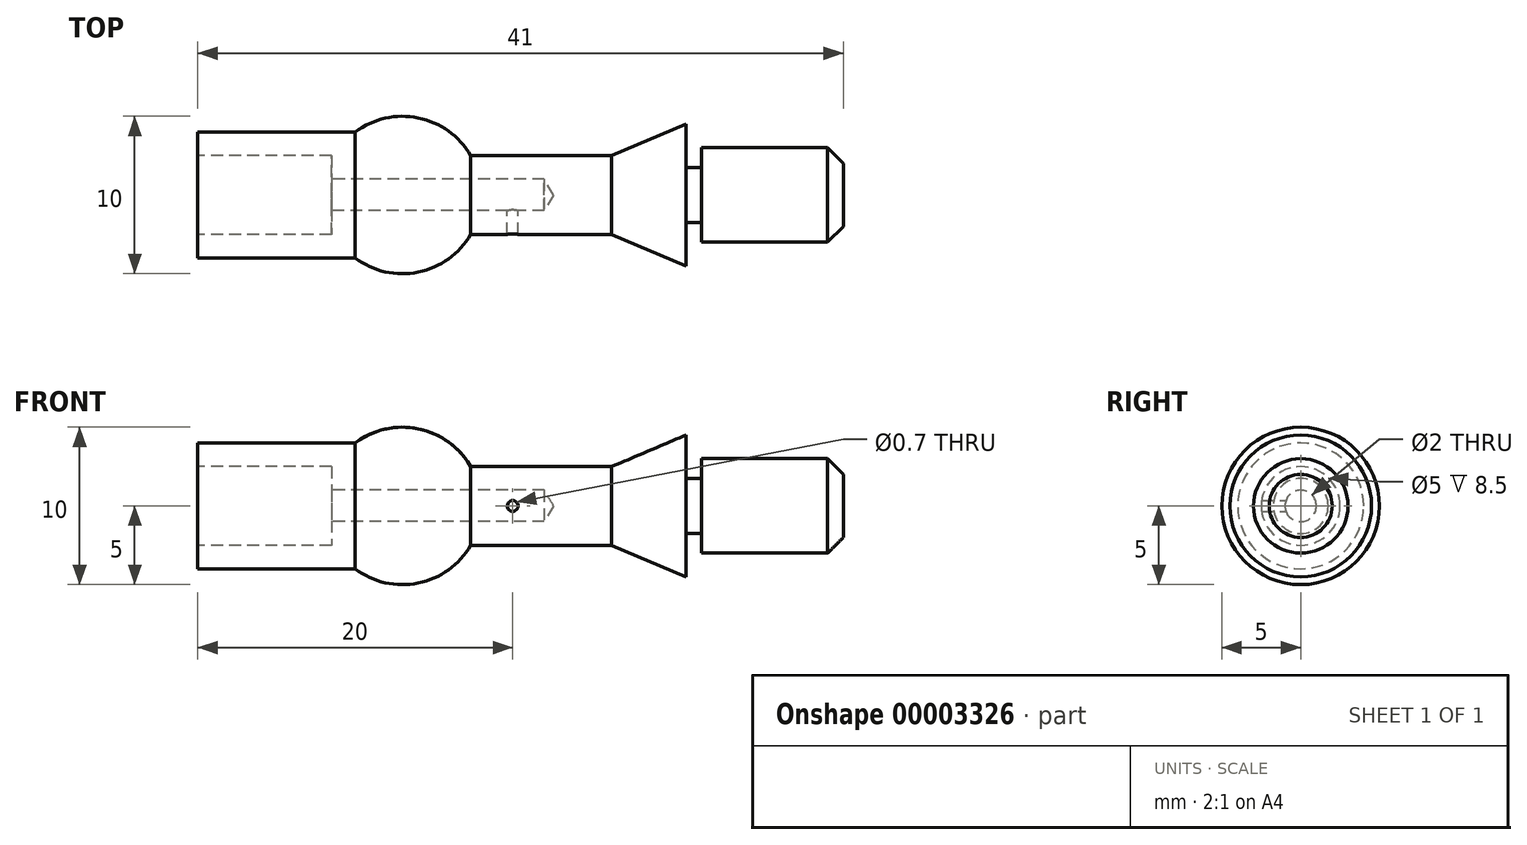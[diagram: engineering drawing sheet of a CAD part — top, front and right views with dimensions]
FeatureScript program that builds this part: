
annotation { "Feature Type Name" : "Feature", "Feature Type Description" : "" }
export const myFeature = defineFeature(function(context is Context, id is Id, definition is map)
    precondition{}
    {
        {
            var Q0;
            Q0=qCreatedBy(makeId("Front.planeOp"),FACE);
            var sketch = newSketch(context, id + "F0", { "sketchPlane" : qUnion([Q0])});
            skLineSegment(sketch, "E0", {"start": v(0, 0) * mm, "end": v(41, 0) * mm, "construction": true});
            skLineSegment(sketch, "E1", {"start": v(0, 2.5) * mm, "end": v(0, 4) * mm});
            skLineSegment(sketch, "E2", {"start": v(0, 4) * mm, "end": v(10, 4) * mm});
            skLineSegment(sketch, "E3", {"start": v(0, 2.5) * mm, "end": v(8.5, 2.5) * mm});
            skLineSegment(sketch, "E4", {"start": v(8.5, 2.5) * mm, "end": v(8.5, 1) * mm});
            skLineSegment(sketch, "E5", {"start": v(8.5, 1) * mm, "end": v(22, 1) * mm});
            skArc(sketch, "E6", {"start": v(17.33, 2.5) * mm, "mid": v(14, 4.9) * mm, "end": v(10, 4) * mm});
            skLineSegment(sketch, "E7", {"start": v(17.33, 2.5) * mm, "end": v(26.29, 2.5) * mm});
            skLineSegment(sketch, "E8", {"start": v(26.29, 2.5) * mm, "end": v(31, 4.5) * mm});
            skLineSegment(sketch, "E9", {"start": v(31, 4.5) * mm, "end": v(31, 1.75) * mm});
            skLineSegment(sketch, "E10", {"start": v(31, -1.75) * mm, "end": v(32, -1.75) * mm});
            skLineSegment(sketch, "E11", {"start": v(32, -3) * mm, "end": v(32, -1.75) * mm});
            skLineSegment(sketch, "E12", {"start": v(32, 3) * mm, "end": v(41, 3) * mm});
            skLineSegment(sketch, "E13", {"start": v(41, 3) * mm, "end": v(41, 0) * mm});
            skLineSegment(sketch, "E14", {"start": v(22, 1) * mm, "end": v(22, 0) * mm, "construction": true});
            skLineSegment(sketch, "E15.0.MirrorCS", {"start": v(22, -1) * mm, "end": v(22, 0) * mm, "construction": true});
            skLineSegment(sketch, "E16.0.MirrorCS", {"start": v(8.5, -1) * mm, "end": v(22, -1) * mm});
            skLineSegment(sketch, "E17.0.MirrorCS", {"start": v(8.5, -2.5) * mm, "end": v(8.5, -1) * mm});
            skLineSegment(sketch, "E18.0.MirrorCS", {"start": v(0, -2.5) * mm, "end": v(8.5, -2.5) * mm});
            skLineSegment(sketch, "E19.0.MirrorCS", {"start": v(0, -2.5) * mm, "end": v(0, -4) * mm});
            skLineSegment(sketch, "E20.0.MirrorCS", {"start": v(0, -4) * mm, "end": v(10, -4) * mm});
            skArc(sketch, "E21.0.MirrorCS", {"start": v(17.33, -2.5) * mm, "mid": v(14, -4.9) * mm, "end": v(10, -4) * mm});
            skLineSegment(sketch, "E22.0.MirrorCS", {"start": v(17.33, -2.5) * mm, "end": v(26.29, -2.5) * mm});
            skLineSegment(sketch, "E23.0.MirrorCS", {"start": v(26.29, -2.5) * mm, "end": v(31, -4.5) * mm});
            skLineSegment(sketch, "E24.0.MirrorCS", {"start": v(31, -4.5) * mm, "end": v(31, -1.75) * mm});
            skLineSegment(sketch, "E25.0.MirrorCS", {"start": v(31, 1.75) * mm, "end": v(32, 1.75) * mm});
            skLineSegment(sketch, "E26.0.MirrorCS", {"start": v(32, 3) * mm, "end": v(32, 1.75) * mm});
            skLineSegment(sketch, "E27.0.MirrorCS", {"start": v(32, -3) * mm, "end": v(41, -3) * mm});
            skLineSegment(sketch, "E28.0.MirrorCS", {"start": v(41, -3) * mm, "end": v(41, 0) * mm});
            skCircle(sketch, "E29", {"center": v(20, 0) * mm, "radius": 0.35 * mm});
            skLineSegment(sketch, "E30", {"start": v(22, 1) * mm, "end": v(22.6, 0) * mm});
            skLineSegment(sketch, "E31", {"start": v(22.6, 0) * mm, "end": v(22, -1) * mm});
            skLineSegment(sketch, "E32", {"start": v(22.6, 0) * mm, "end": v(41, 0) * mm});
            skSolve(sketch);
        }
        {
            var Q0;
            Q0=makeQuery(id+"F0.imprint","IMPRINT",FACE,{"disambiguationData":[TD([[makeQuery(id+"F0.imprint","IMPRINT",EDGE,{"derivedFrom":sQuery(id+"F0.wireOp",EDGE,"E1")}),-1.0]])]});
            var Q1;
            Q1=sQuery(id+"F0.wireOp",EDGE,"E0");
            revolve(context, id + "F1", {"entities" : qUnion([Q0]), "axis" : qUnion([Q1]), "revolveType" : RevolveType.FULL});
        }
        {
            var Q0;
            Q0=makeQuery(id+"F0.imprint","IMPRINT",FACE,{"disambiguationData":[TD([[makeQuery(id+"F0.imprint","IMPRINT",EDGE,{"derivedFrom":sQuery(id+"F0.wireOp",EDGE,"E29")}),1.0]])]});
            extrude(context, id + "F2", {"entities" : qUnion([Q0]), "operationType" : NewBodyOperationType.REMOVE, "endBound" : BoundingType.THROUGH_ALL, "depth" : 25 * mm});
        }
        {
            var Q0;
            Q0=makeQuery(id+"F1.opRevolve","SWEPT_EDGE",EDGE,{"disambiguationData":[OSD([sQuery(id+"F0.wireOp",EDGE,"E12"),sQuery(id+"F0.wireOp",EDGE,"E13")])]});
            chamfer(context, id + "F3", {"entities" : qUnion([Q0]), "width" : 1 * mm, "tangentPropagation" : true});
        }
    });
